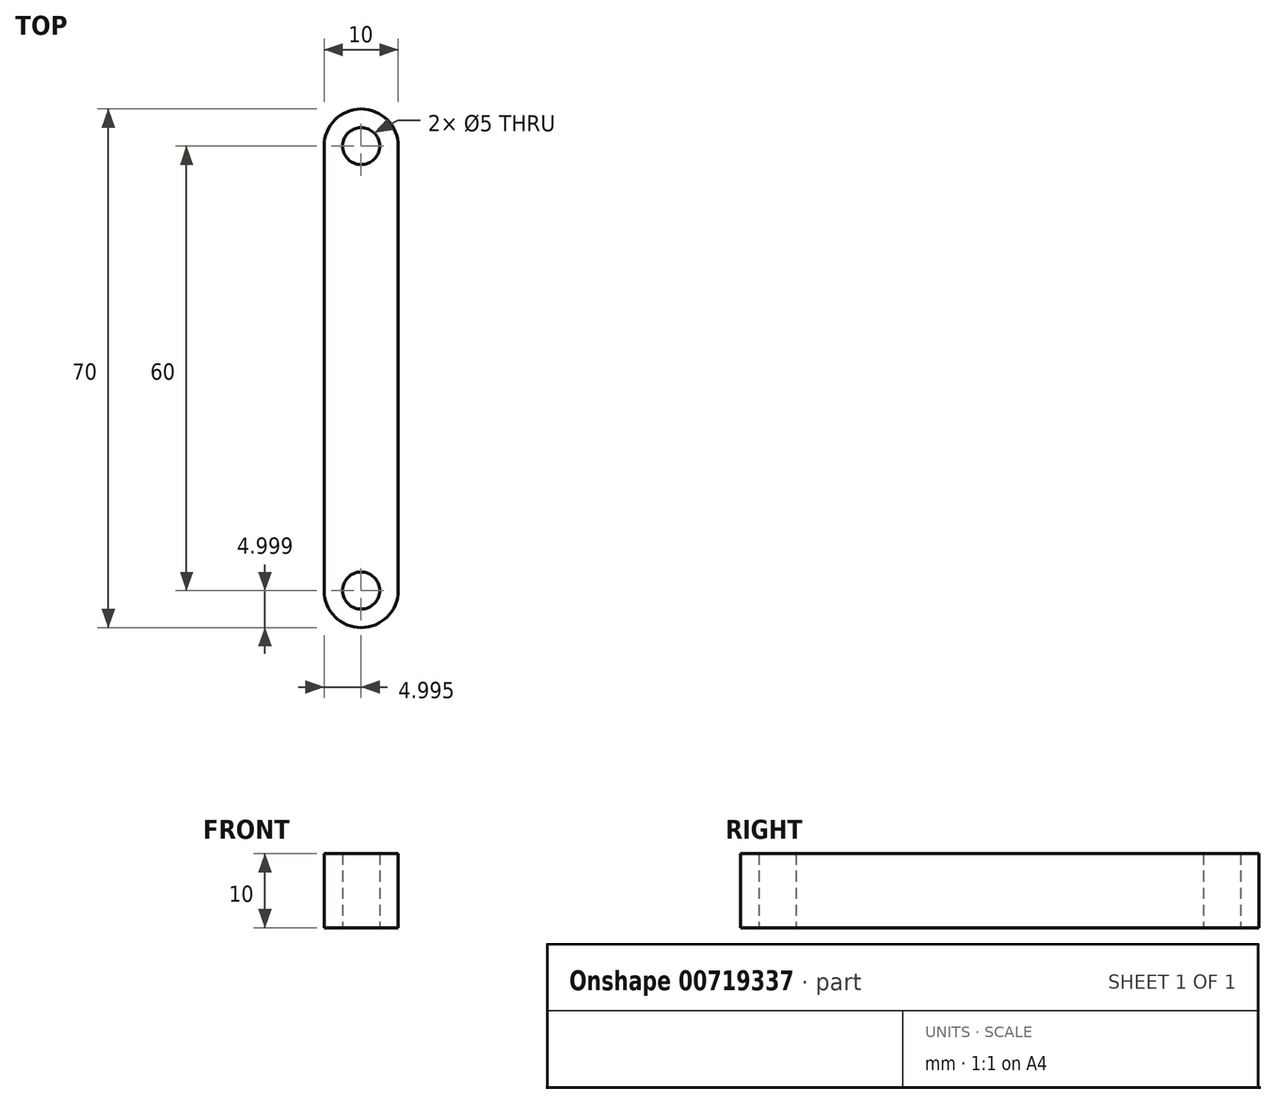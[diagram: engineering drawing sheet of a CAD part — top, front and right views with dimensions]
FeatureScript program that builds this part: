
annotation { "Feature Type Name" : "Feature", "Feature Type Description" : "" }
export const myFeature = defineFeature(function(context is Context, id is Id, definition is map)
    precondition{}
    {
        {
            var Q0;
            Q0=qCreatedBy(makeId("Top.planeOp"),FACE);
            var sketch = newSketch(context, id + "F0", { "sketchPlane" : qUnion([Q0])});
            skLineSegment(sketch, "E0", {"start": v(-15.66, 25.12) * mm, "end": v(-15.66, -34.88) * mm});
            skLineSegment(sketch, "E1", {"start": v(-5.66, -34.88) * mm, "end": v(-5.66, 25.12) * mm});
            skArc(sketch, "E2", {"start": v(-5.66, 25.12) * mm, "mid": v(-10.66, 30.12) * mm, "end": v(-15.66, 25.12) * mm});
            skArc(sketch, "E3", {"start": v(-15.66, -34.88) * mm, "mid": v(-10.66, -39.88) * mm, "end": v(-5.66, -34.88) * mm});
            skCircle(sketch, "E4", {"center": v(-10.66, 25.12) * mm, "radius": 2.5 * mm});
            skCircle(sketch, "E5", {"center": v(-10.66, -34.88) * mm, "radius": 2.5 * mm});
            skSolve(sketch);
        }
        {
            var Q0;
            Q0 = qSketchRegion(id + "F0", true);
            extrude(context, id + "F1", {"entities" : qUnion([Q0]), "depth" : 10 * mm, "offsetDistance" : 25 * mm});
        }
    });
